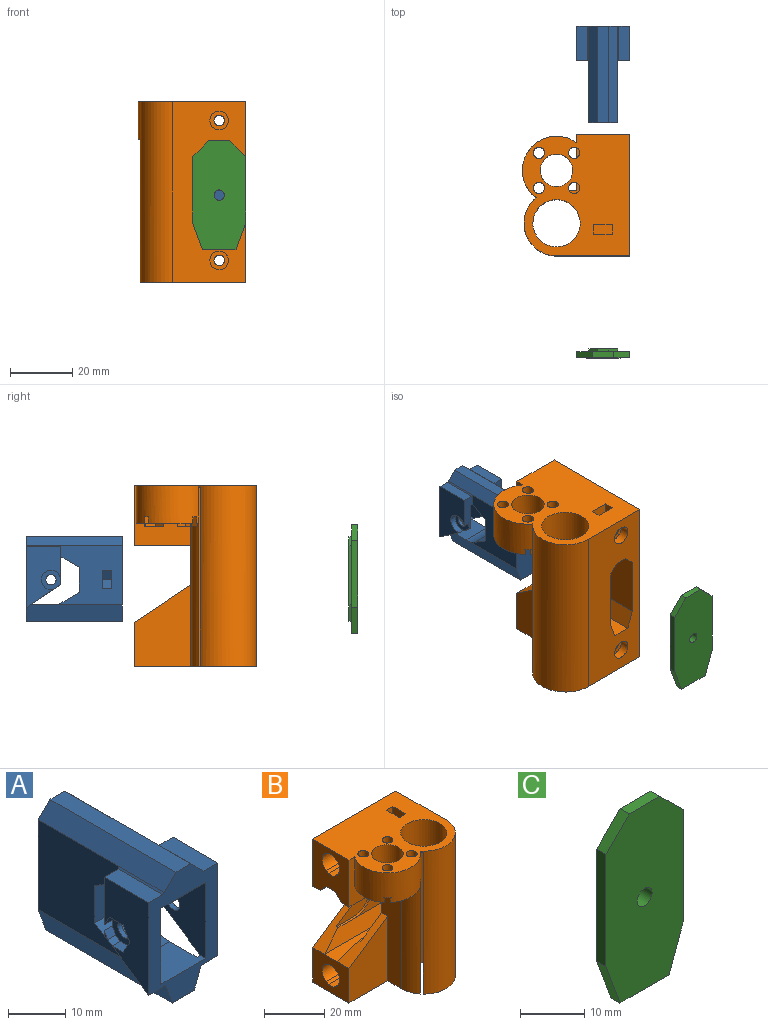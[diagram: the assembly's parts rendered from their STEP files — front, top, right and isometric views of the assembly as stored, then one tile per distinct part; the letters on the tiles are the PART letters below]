
ASSEMBLY  parts=3 mates=3
PART A: 54 faces, bbox 17x31x27.4 mm
  f0: plane 12.6x3.8mm, normal (0,1,0), area 34.9mm2, adj f1,f2,f5,f8,f10,f26,f27,f52
  f1: plane 1x0.6mm, normal (0,0.56,-0.83), area 0.7mm2, adj f0,f5,f27,f49
  f2: plane 19.72x11mm, normal (1,0,0), area 146mm2, adj f0,f14,f26,f48,f52
  f3: plane 19.72x11mm, normal (-1,0,0), area 147mm2, adj f14,f25,f38,f39,f40,f41,f42,f47
  f4: cylinder r=8.09mm len=9.4mm, axis (1,0,0), area 41.8mm2, adj f8,f13,f21,f24
  f5: plane 16.18x11mm, normal (-1,0,0), area 137.3mm2, adj f0,f1,f10,f14,f21,f23,f28,f48
  f6: plane 1.56x0.9mm, normal (-1,0,0), area 0.4mm2, adj f25,f37,f47
  f7: cylinder r=1.65mm len=3.3mm, axis (1,0,0), area 10.4mm2, adj f22,f43
  f8: plane 23x19.13mm, normal (1,0,0), area 295.1mm2, adj f0,f4,f9,f10,f11,f12,f13,f15
  f9: plane 27.4x9.4mm, normal (0,1,0), area 230.1mm2, adj f8,f15,f16,f17,f18,f19,f20,f24
  f10: cylinder r=8.09mm len=11mm, axis (1,0,0), area 46.7mm2, adj f0,f5,f8,f11,f22,f23,f24,f25
  f11: plane 9.4x4.86mm, normal (0,-0.51,-0.86), area 53.2mm2, adj f8,f10,f12,f24
  f12: plane 9.4x8mm, normal (0,-1,0), area 75.2mm2, adj f8,f11,f13,f24
  f13: plane 9.4x4.86mm, normal (0,-0.51,0.86), area 53.2mm2, adj f4,f8,f12,f24
  f14: plane 27.4x17mm, normal (0,-1,0), area 211mm2, adj f2,f3,f5,f15,f16,f17,f18,f19
  f15: plane 31x5.37mm, normal (0.94,0,-0.34), area 176.6mm2, adj f8,f9,f14,f20,f21,f48
  f16: plane 31x2.9mm, normal (0.71,0,0.71), area 126.9mm2, adj f8,f9,f14,f17,f53
  f17: plane 31x3.61mm, normal (0,0,1), area 112mm2, adj f9,f14,f16,f18
  f18: plane 31x2.9mm, normal (-0.71,0,0.71), area 126.9mm2, adj f9,f14,f17,f24,f51
  f19: plane 31x5.37mm, normal (-0.94,0,-0.34), area 176.6mm2, adj f9,f14,f20,f21,f24,f47
  f20: plane 31x5.49mm, normal (0,0,-1), area 170.2mm2, adj f9,f14,f15,f19
  f21: plane 11x8mm, normal (0,0,1), area 77.3mm2, adj f4,f5,f14,f15,f19,f22,f47,f48
  f22: plane 16.18x11mm, normal (1,0,0), area 137.2mm2, adj f7,f10,f14,f21,f23,f25,f47
  f23: plane 11x8mm, normal (0,0,-1), area 88mm2, adj f5,f10,f14,f22
  f24: plane 23x19.13mm, normal (-1,0,0), area 312.5mm2, adj f4,f9,f10,f11,f12,f13,f18,f19
  f25: plane 12.6x3.8mm, normal (0,1,0), area 37.1mm2, adj f3,f6,f10,f22,f24,f37,f42,f43
  f26: cylinder r=3.1mm len=6.2mm, axis (1,0,0), area 29.5mm2, adj f0,f2,f27,f48
  f27: plane 6.2x6.1mm, normal (1,0,0), area 21.7mm2, adj f0,f1,f26,f28,f49
  f28: cylinder r=1.65mm len=3.3mm, axis (1,0,0), area 10.4mm2, adj f5,f27
  f29: plane 8.55x5.8mm, normal (0,-1,0), area 36.2mm2, adj f8,f30,f32,f33,f34,f35,f36,f46
  f30: plane 4.7x3mm, normal (0,0,-1), area 14.1mm2, adj f8,f29,f31,f34
  f31: plane 8.55x5.8mm, normal (0,1,0), area 36.2mm2, adj f8,f30,f32,f33,f34,f35,f36,f45
  f32: plane 4.7x3mm, normal (0,0,1), area 14.1mm2, adj f8,f29,f31,f33
  f33: plane 3x2.17mm, normal (0,0,1), area 6.5mm2, adj f29,f31,f32,f36
  f34: plane 3x2.17mm, normal (0,0,-1), area 6.5mm2, adj f29,f30,f31,f35
  f35: plane 3x2.9mm, normal (0.87,0,-0.5), area 10mm2, adj f29,f31,f34,f36
  f36: plane 3x2.9mm, normal (0.87,0,0.5), area 10mm2, adj f29,f31,f33,f35
  f37: plane 2x1.56mm, normal (0,-0.87,0.5), area 3.6mm2, adj f6,f25,f43,f47
  f38: plane 2.68x2mm, normal (0,0,1), area 5.4mm2, adj f3,f39,f43,f47
  f39: plane 2.9x2mm, normal (0,0.87,0.5), area 6.7mm2, adj f3,f38,f40,f43
  f40: plane 2.9x2mm, normal (0,0.87,-0.5), area 6.7mm2, adj f3,f39,f41,f43
  f41: plane 3.35x2mm, normal (0,0,-1), area 6.7mm2, adj f3,f40,f42,f43
  f42: plane 2.3x2mm, normal (0,-0.87,-0.5), area 5.3mm2, adj f3,f25,f41,f43
  f43: plane 6.35x5.8mm, normal (-1,0,0), area 20.1mm2, adj f7,f25,f37,f38,f39,f40,f41,f42
  f44: plane 3.3x3.3mm, normal (0,1,0), area 8.6mm2, adj f45
  f45: cylinder r=1.65mm len=6.5mm, axis (0,1,0), area 67.4mm2, adj f31,f44
  f46: cylinder r=1.65mm len=3.5mm, axis (0,1,0), area 36.3mm2, adj f9,f29
  f47: plane 11x7.42mm, normal (0,0.56,-0.83), area 38.7mm2, adj f3,f6,f14,f19,f21,f22,f25,f37
  f48: plane 8.91x6.01mm, normal (0,0.56,-0.83), area 33.8mm2, adj f2,f5,f14,f15,f21,f26,f49
  f49: cylinder r=3.1mm len=1.49mm, axis (1,0,0), area 1.8mm2, adj f1,f5,f27,f48
  f50: plane 11x3.5mm, normal (0,0,1), area 38.5mm2, adj f3,f14,f25,f51
  f51: plane 11x0.3mm, normal (-0.71,0,0.71), area 4.7mm2, adj f14,f18,f25,f50
  f52: plane 11x3.5mm, normal (0,0,1), area 38.5mm2, adj f0,f2,f14,f53
  f53: plane 11x0.3mm, normal (0.71,0,0.71), area 4.7mm2, adj f0,f14,f16,f52
PART B: 113 faces, bbox 39.4x34.9x58.4 mm
  f0: plane 46x10mm, normal (-1,0,0), area 331.8mm2, adj f7,f12,f13,f21,f27,f45,f61,f62
  f1: cylinder r=1.8mm len=10mm, axis (0,0,1), area 113.1mm2, adj f26,f84
  f2: cylinder r=1.8mm len=10mm, axis (0,0,1), area 113.1mm2, adj f26,f85
  f3: cylinder r=1.8mm len=10mm, axis (0,0,1), area 113.1mm2, adj f26,f86
  f4: cylinder r=5.25mm len=10.5mm, axis (0,0,1), area 329.9mm2, adj f26,f84,f85,f86,f87
  f5: cylinder r=1.8mm len=10mm, axis (0,0,1), area 113.1mm2, adj f26,f87
  f6: plane 4.38x1.25mm, normal (0,0,-1), area 2.7mm2, adj f13,f93,f94
  f7: plane 4.82x1.61mm, normal (0,0,-1), area 3.1mm2, adj f0,f27,f95,f96,f109
  f8: plane 13.63x5.75mm, normal (0,0,-1), area 38.4mm2, adj f13,f71,f88,f89,f90,f91,f92,f102
  f9: plane 0.92x0.49mm, normal (0,0,-1), area 0.2mm2, adj f27,f71,f110
  f10: plane 18.05x12.18mm, normal (-0.56,0,0.83), area 77.1mm2, adj f23,f24,f48,f59,f79,f81
  f11: cylinder r=10.47mm len=58mm, axis (0,0,-1), area 1440.3mm2, adj f12,f25,f26,f71,f74,f75
  f12: plane 39x33.98mm, normal (0,0,-1), area 768.5mm2, adj f0,f11,f21,f23,f24,f25,f27,f28
  f13: plane 19.07x18.05mm, normal (0,-1,0), area 148.8mm2, adj f0,f6,f8,f22,f26,f61,f71,f82
  f14: cylinder r=1.7mm len=3.4mm, axis (1,0,0), area 16mm2, adj f32,f67
  f15: plane 3.16x0.39mm, normal (-1,0,0), area 0.4mm2, adj f55,f56,f58,f70
  f16: plane 20.42x2.81mm, normal (0,0,1), area 47.6mm2, adj f17,f19,f20,f22,f54,f66
  f17: plane 20.02x0.89mm, normal (0,0.71,0.71), area 24.3mm2, adj f16,f18,f20,f22,f65,f66
  f18: cylinder r=4.07mm len=19.6mm, axis (-1,0,0), area 416.8mm2, adj f17,f19,f22,f65
  f19: plane 20.02x0.89mm, normal (0,-0.71,0.71), area 24.3mm2, adj f16,f18,f22,f54,f65,f66
  f20: plane 0.46x0.12mm, normal (-1,0,0), area 0mm2, adj f16,f17,f66
  f21: plane 26.18x18.05mm, normal (0,-1,0), area 362.6mm2, adj f0,f12,f24,f62
  f22: plane 19.07x17mm, normal (-1,0,0), area 249.5mm2, adj f13,f16,f17,f18,f19,f23,f26,f42
  f23: plane 58x39mm, normal (0,1,0), area 1921.9mm2, adj f10,f12,f22,f24,f25,f26,f59,f60
  f24: plane 17x14mm, normal (-1,0,0), area 184.6mm2, adj f10,f12,f21,f23,f47,f55,f56,f57
  f25: plane 58x23.5mm, normal (1,0,0), area 1047.4mm2, adj f11,f12,f23,f26,f42,f43,f44,f45
  f26: plane 39x34.5mm, normal (0,0,1), area 923.6mm2, adj f1,f2,f3,f4,f5,f11,f13,f22
  f27: cylinder r=10.47mm len=46mm, axis (0,0,-1), area 321.8mm2, adj f0,f7,f9,f12,f73,f109,f110,f112
  f28: cylinder r=7.62mm len=58mm, axis (0,0,-1), area 2717.6mm2, adj f12,f26,f73,f74,f75
  f29: plane 10.6x3mm, normal (0,1,0), area 31.8mm2, adj f12,f30,f32,f33
  f30: plane 10.6x6mm, normal (-1,0,0), area 54.5mm2, adj f12,f29,f31,f33,f41
  f31: plane 10.6x3mm, normal (0,-1,0), area 31.8mm2, adj f12,f30,f32,f33
  f32: plane 10.6x6mm, normal (1,0,0), area 54.5mm2, adj f12,f14,f29,f31,f33
  f33: plane 6x3mm, normal (0,0,-1), area 18mm2, adj f29,f30,f31,f32
  f34: plane 9.1x3mm, normal (0,1,0), area 27.3mm2, adj f26,f35,f37,f38
  f35: plane 9.1x6mm, normal (-1,0,0), area 45.5mm2, adj f26,f34,f36,f38,f40
  f36: plane 9.1x3mm, normal (0,-1,0), area 27.3mm2, adj f26,f35,f37,f38
  f37: plane 9.1x6mm, normal (1,0,0), area 45.5mm2, adj f26,f34,f36,f38,f39
  f38: plane 6x3mm, normal (0,0,1), area 18mm2, adj f34,f35,f36,f37
  f39: cylinder r=1.7mm len=3.4mm, axis (1,0,0), area 16mm2, adj f37,f64
  f40: cylinder r=1.7mm len=4mm, axis (1,0,0), area 42.7mm2, adj f35,f53
  f41: cylinder r=1.7mm len=4mm, axis (1,0,0), area 42.7mm2, adj f30,f51
  f42: plane 39x3.07mm, normal (0,-0.71,-0.71), area 169.4mm2, adj f22,f25,f43,f49,f60
  f43: plane 39x3.86mm, normal (0,0,-1), area 150.5mm2, adj f22,f25,f42,f44
  f44: plane 39x3.07mm, normal (0,0.71,-0.71), area 169.4mm2, adj f22,f25,f43,f45,f61
  f45: plane 23x19.31mm, normal (0,1,0), area 333.7mm2, adj f0,f25,f44,f46,f76
  f46: plane 39x5.62mm, normal (0,0.94,0.34), area 208.3mm2, adj f25,f45,f47,f62,f78
  f47: plane 39x5.91mm, normal (0,0,1), area 230.5mm2, adj f24,f25,f46,f48
  f48: plane 39x5.62mm, normal (0,-0.94,0.34), area 208.3mm2, adj f10,f25,f47,f49,f79
  f49: plane 23x19.31mm, normal (0,-1,0), area 333.7mm2, adj f25,f42,f48,f59,f80
  f50: cylinder r=3mm len=6mm, axis (1,0,0), area 56.5mm2, adj f25,f51
  f51: plane 6x6mm, normal (1,0,0), area 19.2mm2, adj f41,f50
  f52: cylinder r=3mm len=6mm, axis (1,0,0), area 56.5mm2, adj f25,f53
  f53: plane 6x6mm, normal (1,0,0), area 19.2mm2, adj f40,f52
  f54: plane 0.46x0.12mm, normal (-1,0,0), area 0mm2, adj f16,f19,f66
  f55: plane 20x2.39mm, normal (0,0,1), area 47.8mm2, adj f15,f24,f56,f58
  f56: plane 20x0.87mm, normal (0,0.71,0.71), area 24.7mm2, adj f15,f24,f55,f57,f68
  f57: cylinder r=4.07mm len=20mm, axis (-1,0,0), area 425.3mm2, adj f24,f56,f58,f68
  f58: plane 20x0.87mm, normal (0,-0.71,0.71), area 24.7mm2, adj f15,f24,f55,f57,f68
  f59: plane 12.75x3.5mm, normal (-1,0,0), area 37.1mm2, adj f10,f23,f49,f60,f80,f81
  f60: plane 18.05x3.5mm, normal (0,0,-1), area 63.2mm2, adj f22,f23,f42,f59
  f61: plane 18.05x3.5mm, normal (0,0,-1), area 63.2mm2, adj f0,f13,f22,f44
  f62: plane 18.05x12.18mm, normal (-0.56,0,0.83), area 77.1mm2, adj f0,f21,f24,f46,f77,f78
  f63: cylinder r=5.5mm len=11mm, axis (-1,0,0), area 172.8mm2, adj f64,f66
  f64: plane 11x11mm, normal (-1,0,0), area 86mm2, adj f39,f63
  f65: plane 8.6x8.3mm, normal (1,0,0), area 5.1mm2, adj f17,f18,f19,f66
  f66: cone r=5.5mm half-angle=22.5deg, axis (1,0,0), area 95.3mm2, adj f16,f17,f19,f20,f54,f63,f65
  f67: plane 11x11mm, normal (-1,0,0), area 86mm2, adj f14,f69
  f68: plane 8.6x8.3mm, normal (1,0,0), area 5.1mm2, adj f56,f57,f58,f70
  f69: cylinder r=5.5mm len=11mm, axis (-1,0,0), area 172.8mm2, adj f67,f70
  f70: cone r=5.5mm half-angle=25.6deg, axis (1,0,0), area 85.4mm2, adj f15,f68,f69
  f71: cylinder r=11mm len=19.83mm, axis (0,0,1), area 407mm2, adj f8,f9,f11,f13,f26,f72,f73,f86
  f72: plane 14.3x5.75mm, normal (0,0,-1), area 38.5mm2, adj f71,f97,f98,f99,f100,f101,f111
  f73: plane 57.5x2.15mm, normal (0.66,-0.75,0), area 164.7mm2, adj f12,f27,f28,f71,f75
  f74: plane 57.5x2.15mm, normal (-0.66,0.75,0), area 164.7mm2, adj f11,f12,f28,f75
  f75: plane 2.81x2.65mm, normal (0,0,-1), area 2.9mm2, adj f11,f28,f73,f74
  f76: cylinder r=8.14mm len=16.02mm, axis (0,1,0), area 18.8mm2, adj f0,f45,f77,f78
  f77: plane 16.02x15.81mm, normal (0,1,0), area 102.7mm2, adj f0,f62,f76,f78
  f78: plane 7.67x0.8mm, normal (0,0,1), area 6.1mm2, adj f46,f62,f76,f77
  f79: plane 7.67x0.8mm, normal (0,0,1), area 6.1mm2, adj f10,f48,f80,f81
  f80: cylinder r=8.14mm len=16.02mm, axis (0,-1,0), area 18.8mm2, adj f49,f59,f79,f81
  f81: plane 16.02x15.81mm, normal (0,-1,0), area 102.7mm2, adj f10,f59,f79,f80
  f82: plane 6.29x2.49mm, normal (0,0,1), area 10.2mm2, adj f13,f92,f93,f103,f104
  f83: plane 6.87x6.83mm, normal (0,0,1), area 17.5mm2, adj f0,f13,f94,f95,f105,f106,f107,f108
  f84: plane 8.92x8.92mm, normal (0,0,-1), area 24.8mm2, adj f1,f4,f90,f91,f92,f93,f103,f104
  f85: plane 9.09x9.09mm, normal (0,0,-1), area 25.4mm2, adj f2,f4,f94,f95,f105,f106,f107,f108
  f86: plane 9.09x9.09mm, normal (0,0,-1), area 25mm2, adj f3,f4,f71,f88,f89,f99,f100,f101
  f87: plane 8.92x8.92mm, normal (0,0,-1), area 24.4mm2, adj f4,f5,f71,f96,f97,f98,f109,f110
  f88: plane 2.46x2.42mm, normal (0.71,-0.7,0), area 6.9mm2, adj f8,f86,f89,f102
  f89: plane 2.39x2mm, normal (0.87,-0.49,0), area 5.5mm2, adj f8,f86,f88,f90
  f90: plane 2.25x2mm, normal (0.87,0.5,0), area 5.2mm2, adj f8,f84,f89,f91
  f91: plane 2.44x2.44mm, normal (0.71,0.71,0), area 6.9mm2, adj f8,f84,f90,f92
  f92: plane 3.33x3mm, normal (0.97,-0.26,0), area 8.6mm2, adj f8,f13,f82,f84,f91,f103
  f93: plane 3x2.25mm, normal (-0.5,-0.87,0), area 5.3mm2, adj f6,f13,f82,f84,f94,f104
  f94: plane 3x2.39mm, normal (0.49,-0.87,0), area 5.7mm2, adj f6,f13,f83,f85,f93,f105
  f95: plane 3x2.39mm, normal (-0.87,0.49,0), area 5.6mm2, adj f0,f7,f83,f85,f96,f108
  f96: plane 2.25x2mm, normal (-0.87,-0.5,0), area 5.2mm2, adj f7,f87,f95,f109
  f97: plane 2.44x2.44mm, normal (0.71,0.71,0), area 6.9mm2, adj f72,f87,f98,f111
  f98: plane 2.25x2mm, normal (0.5,0.87,0), area 5.2mm2, adj f72,f87,f97,f99
  f99: plane 2.39x2mm, normal (-0.49,0.87,0), area 5.5mm2, adj f72,f86,f98,f100
  f100: plane 2.46x2.42mm, normal (-0.7,0.71,0), area 6.9mm2, adj f72,f86,f99,f101
  f101: plane 2.35x2mm, normal (0.26,0.97,0), area 4.9mm2, adj f71,f72,f86,f100
  f102: plane 2.35x2mm, normal (0.97,0.26,0), area 4.9mm2, adj f8,f71,f86,f88
  f103: plane 3.33x3mm, normal (0.26,-0.97,0), area 10.3mm2, adj f82,f84,f92,f104
  f104: plane 3x2.44mm, normal (-0.71,-0.71,0), area 10.4mm2, adj f82,f84,f93,f103
  f105: plane 3x2.46mm, normal (0.7,-0.71,0), area 10.3mm2, adj f83,f85,f94,f106
  f106: plane 3.33x3mm, normal (-0.26,-0.97,0), area 10.4mm2, adj f83,f85,f105,f107
  f107: plane 3.33x3mm, normal (-0.97,-0.26,0), area 10.4mm2, adj f83,f85,f106,f108
  f108: plane 3x2.46mm, normal (-0.71,0.7,0), area 10.3mm2, adj f83,f85,f95,f107
  f109: plane 3x2.44mm, normal (-0.71,-0.71,0), area 9.9mm2, adj f7,f27,f87,f96,f110,f112
  f110: plane 3x2.4mm, normal (-0.97,0.26,0), area 6.5mm2, adj f9,f27,f71,f87,f109,f112
  f111: plane 2.4x2mm, normal (-0.26,0.97,0), area 5mm2, adj f71,f72,f87,f97
  f112: plane 3.61x2.13mm, normal (0,0,1), area 2.5mm2, adj f27,f109,f110
PART C: 20 faces, bbox 17x3x35 mm
  f0: plane 5.12x5.12mm, normal (0.71,0,0.71), area 14.5mm2, adj f1,f7,f8,f9
  f1: plane 6.76x2mm, normal (0,0,1), area 13.5mm2, adj f0,f2,f8,f9
  f2: plane 5.12x5.12mm, normal (-0.71,0,0.71), area 14.5mm2, adj f1,f3,f8,f9
  f3: plane 21.38x2mm, normal (-1,0,0), area 42.8mm2, adj f2,f4,f8,f9
  f4: plane 8.5x3.09mm, normal (-0.94,0,-0.34), area 18.1mm2, adj f3,f5,f8,f9
  f5: plane 10.81x2mm, normal (0,0,-1), area 21.6mm2, adj f4,f6,f8,f9
  f6: plane 8.5x3.09mm, normal (0.94,0,-0.34), area 18.1mm2, adj f5,f7,f8,f9
  f7: plane 21.38x2mm, normal (1,0,0), area 42.8mm2, adj f0,f6,f8,f9
  f8: plane 35x17mm, normal (0,-1,0), area 533.9mm2, adj f0,f1,f2,f3,f4,f5,f6,f7
  f9: plane 35x17mm, normal (0,1,0), area 310.5mm2, adj f0,f1,f2,f3,f4,f5,f6,f7
  f10: plane 2.84x2.84mm, normal (-0.71,0,0.71), area 3.8mm2, adj f9,f11,f16,f19
  f11: plane 19.07x0.95mm, normal (-1,0,0), area 18.1mm2, adj f9,f10,f12,f19
  f12: plane 5.29x1.93mm, normal (-0.94,0,-0.34), area 5.3mm2, adj f9,f11,f13,f19
  f13: plane 5.35x0.95mm, normal (0,0,-1), area 5.1mm2, adj f9,f12,f14,f19
  f14: plane 5.29x1.93mm, normal (0.94,0,-0.34), area 5.3mm2, adj f9,f13,f15,f19
  f15: plane 19.07x0.95mm, normal (1,0,0), area 18.1mm2, adj f9,f14,f17,f19
  f16: plane 3.53x0.95mm, normal (0,0,1), area 3.4mm2, adj f9,f10,f17,f19
  f17: plane 2.84x2.84mm, normal (0.71,0,0.71), area 3.8mm2, adj f9,f15,f16,f19
  f18: cylinder r=1.65mm len=3.3mm, axis (0,1,0), area 30.6mm2, adj f8,f19
  f19: plane 27.2x9.2mm, normal (0,1,0), area 223.5mm2, adj f10,f11,f12,f13,f14,f15,f16,f17
PLACE A rot(axis=(0,0,-1),180deg) t=(19.24,-34.72,7.62)mm
PLACE B rot(axis=(0,0,-1),90deg) t=(4.24,-67.2,-6.38)mm fixed
PLACE C t=(19.24,-108.45,21.62)mm
MATE parallel C.f9 <-> B.f25  axis (0,1,0) through (19.24,-108.45,39.12)mm
MATE slider C.f18 <-> A.f45  axis (0,1,0) through (19.24,-107.5,21.62)mm
MATE slider B.f25 <-> A.f9  axis (0,-1,0) through (19.24,-77.68,7.62)mm
